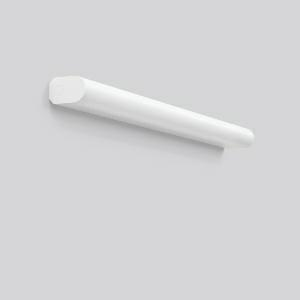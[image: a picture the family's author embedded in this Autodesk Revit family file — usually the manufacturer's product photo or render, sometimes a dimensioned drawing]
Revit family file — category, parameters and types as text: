
# Revit family: rt_44_451169_002_1_62c5
name_source: partatom
category: Lighting Fixtures
units: mm (PartAtom-declared; Revit-internal decimal feet)

## family parameters
Cut with Voids When Loaded = No
Host = Face
Light Source = No
Part Type = Normal
Room Calculation Point = No
Round Connector Dimension = Use Diameter
Shared = No

## types (1)
- RT 44 (1 x LED Modul 840, 1500 lm, 4000)
    Apparent Load = 15 VA
    CIE Flux Codes = 36 65 85 81 100
    Color Rendering = 80
    Color Temperature = 4000
    Default Elevation = 1800 mm
    Description = Series: RT 44
Linear luminaire, can be used as wall and mirror luminaire. Base: aluminium, powder-coated. End caps: plastic (polycarbonate), shock-resistant. Diffuser: plastic (polycarbonate), opal. Suitable for Ceiling mounting, Wall (surface). Can be installed horizontally and vertically. Very easy installation thanks to Plug+Play connection. Driver integrated. High type of protection: IP44 for use in wet areas. 
Colour: pure white (RAL 9010)
Length: 900 mm
Width: 55 mm
Height: 87 mm
Lamp: LED
Socket: without socket
Colour temperature: 4000K
Colour rendering index (CRI): 80
System power: 15 W
Rated luminous flux: 1500 lm
Luminous efficiency: 100 lm/W
Control gear: Regulated power supply
Protection class: I
Type of protection: IP 44
    Height = 87 mm
    Lamp = 1 x LED Modul 840
    Lamp Light Flux = 1500 lm
    Lamp count = 1
    Length = 900 mm
    Lifetime = 50000 h
    Luminous efficacy = 100 lm/W
    Manufacturer = RZB
    ModVariant = No
    Model = 451169.002.1
    Mounting Place = Ceiling, Wall
    Mounting Type = Surface mounted
    Number of Poles = 1
    OnlyDefault = Yes
    Power Factor = 1
    Product Name = RT 44
    Product group = Surface mounted ceiling and wall luminaires
    ProductGroupID = 305
    Protection Class = Protection class I
    Protection Degree = IP 44
    RLX_Detail_Level = 1
    RLX_Emergency_Light_Flux = 0 lm
    RLX_Emergency_Type = 0
    RLX_Emergency_Type_DB = No
    RlxData = <blob elided: 26777 chars, md5=47a1c227>
    Socket = socket
    Standby Power = 0 W
    System Light Flux = 1500 lm
    System Power = 15 W
    Type Comments = Product without accessories
    Type Image = 451055.752.jpg
    URL = http://relux.com
    VarID = ---
    Voltage = 230 V
    Voltage Range = 220-240 V
    Weight = 0.00 kg
    Width = 55 mm

## geometry (parser evidence)
native form markers: Blend x4, Sweep x12
no freeform markers — native parametric forms only
